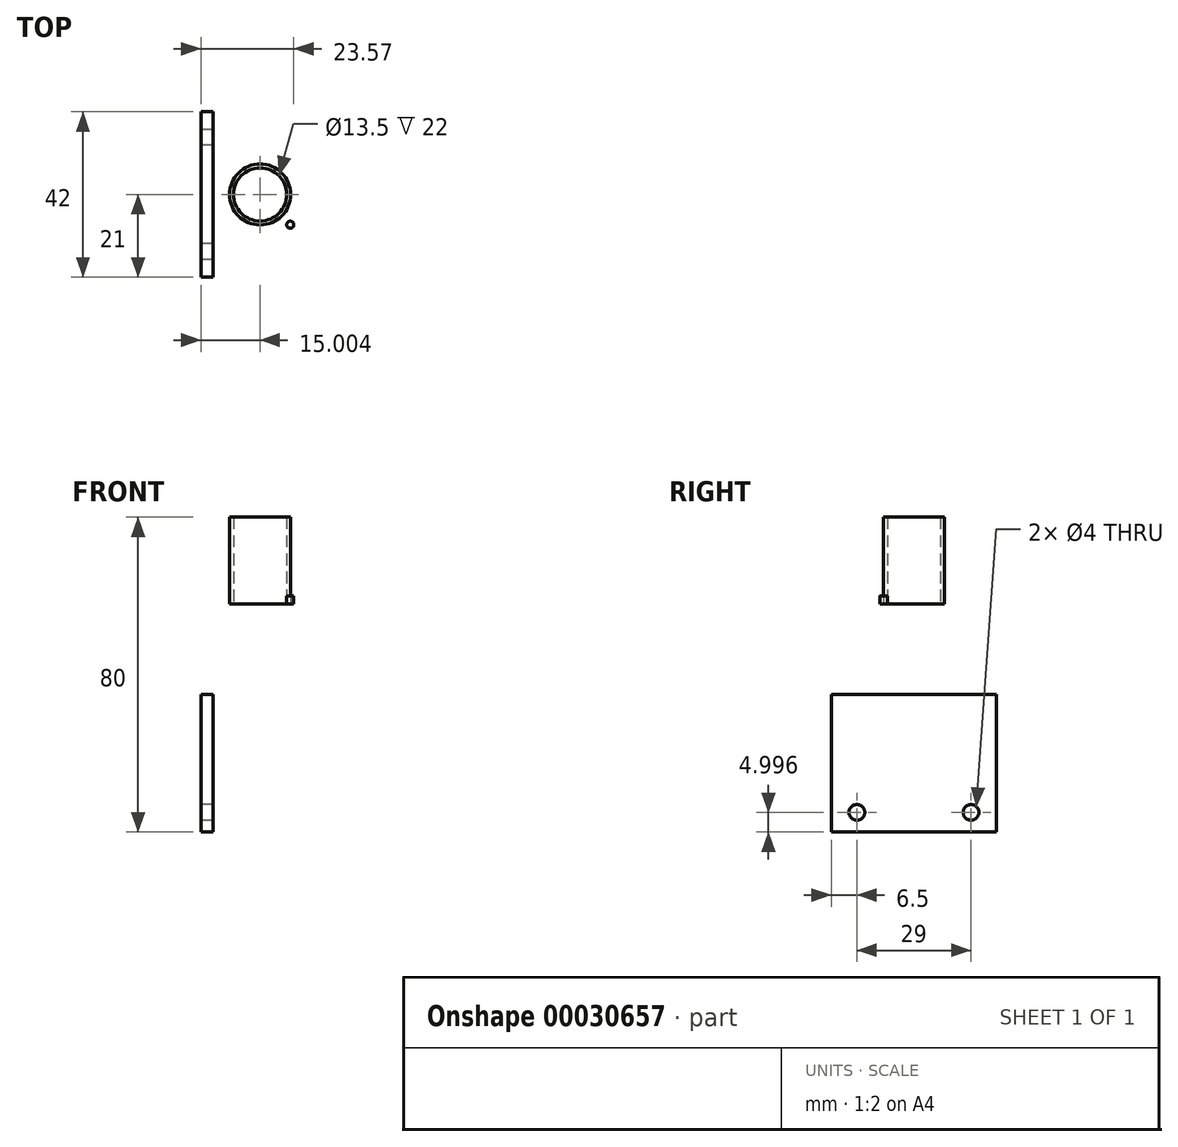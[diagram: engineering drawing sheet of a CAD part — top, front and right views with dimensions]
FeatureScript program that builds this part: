
annotation { "Feature Type Name" : "Feature", "Feature Type Description" : "" }
export const myFeature = defineFeature(function(context is Context, id is Id, definition is map)
    precondition{}
    {
        {
            var Q0;
            Q0=qCreatedBy(makeId("Front.planeOp"),FACE);
            var sketch = newSketch(context, id + "F0", { "sketchPlane" : qUnion([Q0])});
            skLineSegment(sketch, "E0.bottom", {"start": v(-64.57, 3.48) * mm, "end": v(-61.57, 3.48) * mm});
            skLineSegment(sketch, "E0.top", {"start": v(-64.57, -56.52) * mm, "end": v(-61.57, -56.52) * mm});
            skLineSegment(sketch, "E0.left", {"start": v(-64.57, 3.48) * mm, "end": v(-64.57, -56.52) * mm});
            skLineSegment(sketch, "E0.right", {"start": v(-61.57, 3.48) * mm, "end": v(-61.57, -56.52) * mm});
            skSolve(sketch);
        }
        {
            var Q0;
            Q0 = qSketchRegion(id + "F0", true);
            extrude(context, id + "F1", {"entities" : qUnion([Q0]), "depth" : 42 * mm});
        }
        {
            var Q0;
            Q0=qCreatedBy(makeId("Front.planeOp"),FACE);
            var sketch = newSketch(context, id + "F2", { "sketchPlane" : qUnion([Q0])});
            skLineSegment(sketch, "E1.bottom", {"start": v(-64.57, 3.48) * mm, "end": v(-34.57, 3.48) * mm});
            skLineSegment(sketch, "E1.top", {"start": v(-64.57, 1.48) * mm, "end": v(-34.57, 1.48) * mm});
            skLineSegment(sketch, "E1.left", {"start": v(-64.57, 3.48) * mm, "end": v(-64.57, 1.48) * mm});
            skLineSegment(sketch, "E1.right", {"start": v(-34.57, 3.48) * mm, "end": v(-34.57, 1.48) * mm});
            skPoint(sketch, "E2", {"position": v(-58.57, 3.48) * mm});
            skSolve(sketch);
        }
        {
            var Q0;
            Q0 = qSketchRegion(id + "F2", true);
            extrude(context, id + "F3", {"entities" : qUnion([Q0]), "operationType" : NewBodyOperationType.ADD, "depth" : 42 * mm});
        }
        {
            var Q0;
            Q0=makeQuery(id+"F3.opExtrude","SWEPT_FACE",FACE,{"disambiguationData":[OSD([sQuery(id+"F2.wireOp",EDGE,"E1.bottom")])]});
            var sketch = newSketch(context, id + "F4", { "sketchPlane" : qUnion([Q0])});
            skPoint(sketch, "E3", {"position": v(-43.57, -21) * mm});
            skCircle(sketch, "E4", {"center": v(-43.57, -21) * mm, "radius": 7.5 * mm});
            skSolve(sketch);
        }
        {
            var Q0;
            Q0 = qSketchRegion(id + "F4", true);
            var Q1;
            Q1=makeQuery(id+"F4.imprint","IMPRINT",FACE,{"disambiguationData":[TD([[makeQuery(id+"F4.imprint","IMPRINT",EDGE,{"derivedFrom":sQuery(id+"F4.wireOp",EDGE,"E4")}),-1.0]])]});
            extrude(context, id + "F5", {"entities" : qUnion([Q0, Q1]), "operationType" : NewBodyOperationType.ADD, "oppositeDirection" : true, "depth" : 2 * mm});
        }
        {
            var Q0;
            Q0=makeQuery(id+"F3.opExtrude","SWEPT_FACE",FACE,{"disambiguationData":[OSD([sQuery(id+"F2.wireOp",EDGE,"E1.bottom")])]});
            var sketch = newSketch(context, id + "F6", { "sketchPlane" : qUnion([Q0])});
            skLineSegment(sketch, "E5", {"start": v(-34.57, -42) * mm, "end": v(-34.57, 0) * mm});
            skLineSegment(sketch, "E6", {"start": v(-49.57, 0) * mm, "end": v(-49.57, -42) * mm, "construction": true});
            skCircle(sketch, "E7", {"center": v(-49.57, -21) * mm, "radius": 7.75 * mm});
            skCircle(sketch, "E8", {"center": v(-49.57, -21) * mm, "radius": 6.75 * mm});
            skSolve(sketch);
        }
        {
            var Q0;
            Q0 = qSketchRegion(id + "F6", true);
            extrude(context, id + "F7", {"entities" : qUnion([Q0]), "operationType" : NewBodyOperationType.ADD, "depth" : 20 * mm});
        }
        {
            var Q0;
            Q0=makeQuery(id+"F3.opExtrude","SWEPT_FACE",FACE,{"disambiguationData":[OSD([sQuery(id+"F2.wireOp",EDGE,"E1.bottom")])]});
            var sketch = newSketch(context, id + "F8", { "sketchPlane" : qUnion([Q0])});
            skPoint(sketch, "E9", {"position": v(-49.57, 0) * mm});
            skPoint(sketch, "E10", {"position": v(-49.57, -42) * mm});
            skPoint(sketch, "E11", {"position": v(-57.24, -28.7) * mm});
            skCircle(sketch, "E12", {"center": v(-57.24, -28.7) * mm, "radius": 0.9 * mm});
            skPoint(sketch, "E13", {"position": v(-49.57, -21) * mm});
            skPoint(sketch, "E14.MirrorP", {"position": v(-41.9, -28.7) * mm});
            skCircle(sketch, "E15.MirrorC", {"center": v(-41.9, -28.7) * mm, "radius": 0.9 * mm});
            skLineSegment(sketch, "E16", {"start": v(-41.8, -20.96) * mm, "end": v(-41.9, -22.4) * mm, "construction": true});
            skLineSegment(sketch, "E17", {"start": v(-41.8, -20.96) * mm, "end": v(-41.9, -28.7) * mm, "construction": true});
            skLineSegment(sketch, "E18", {"start": v(-50.45, -28.7) * mm, "end": v(-41.9, -28.7) * mm, "construction": true});
            skSolve(sketch);
        }
        {
            var Q0;
            Q0=makeQuery(id+"F1.opExtrude","SWEPT_FACE",FACE,{"disambiguationData":[OSD([sQuery(id+"F0.wireOp",EDGE,"E0.left")])]});
            var sketch = newSketch(context, id + "F9", { "sketchPlane" : qUnion([Q0])});
            skLineSegment(sketch, "E19", {"start": v(0, -51.52) * mm, "end": v(42, -51.52) * mm, "construction": true});
            skCircle(sketch, "E20", {"center": v(35.5, -51.52) * mm, "radius": 2 * mm});
            skCircle(sketch, "E21", {"center": v(6.5, -51.52) * mm, "radius": 2 * mm});
            skSolve(sketch);
        }
        {
            var Q0;
            Q0 = qSketchRegion(id + "F9", true);
            extrude(context, id + "F10", {"entities" : qUnion([Q0]), "operationType" : NewBodyOperationType.REMOVE, "oppositeDirection" : true, "depth" : 25 * mm});
        }
        {
            var Q0;
            Q0=makeQuery(id+"F6.imprint","IMPRINT",FACE,{"disambiguationData":[TD([[makeQuery(id+"F6.imprint","IMPRINT",EDGE,{"derivedFrom":sQuery(id+"F6.wireOp",EDGE,"E8")}),1.0]])]});
            extrude(context, id + "F11", {"entities" : qUnion([Q0]), "operationType" : NewBodyOperationType.REMOVE, "oppositeDirection" : true, "depth" : 25 * mm});
        }
        {
            var Q0;
            Q0=makeQuery(id+"F8.imprint","IMPRINT",FACE,{"disambiguationData":[TD([[makeQuery(id+"F8.imprint","IMPRINT",EDGE,{"derivedFrom":sQuery(id+"F8.wireOp",EDGE,"E12")}),1.0]])]});
            var Q1;
            Q1=makeQuery(id+"F8.imprint","IMPRINT",FACE,{"disambiguationData":[TD([[makeQuery(id+"F8.imprint","IMPRINT",EDGE,{"derivedFrom":sQuery(id+"F8.wireOp",EDGE,"E15.MirrorC")}),-1.0]])]});
            extrude(context, id + "F12", {"entities" : qUnion([Q0, Q1]), "operationType" : NewBodyOperationType.REMOVE, "oppositeDirection" : true, "depth" : 25 * mm});
        }
    });
